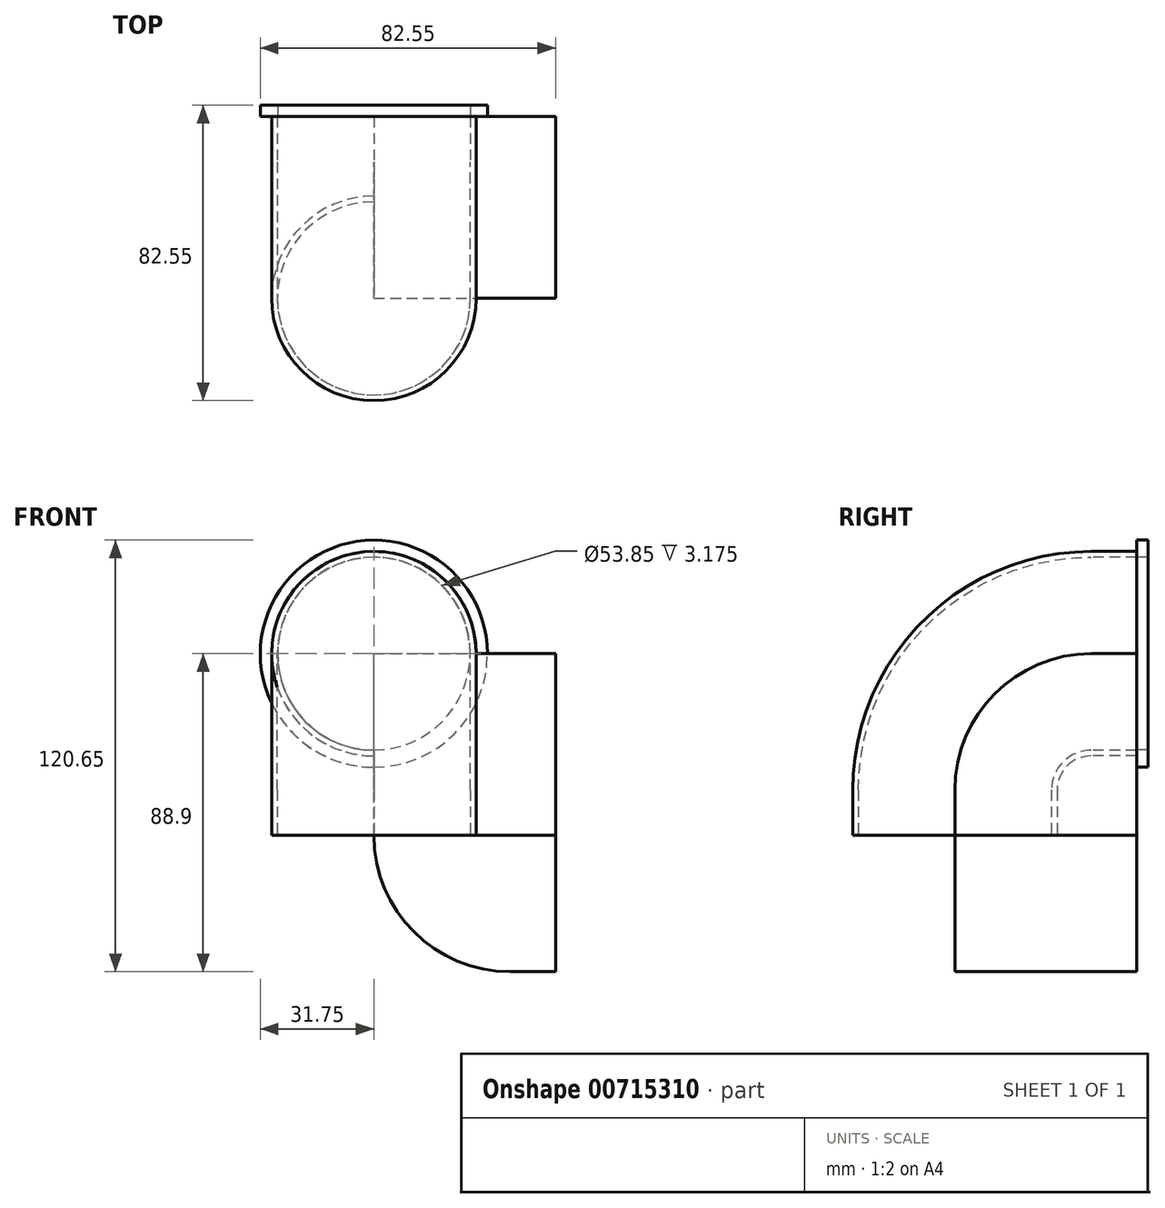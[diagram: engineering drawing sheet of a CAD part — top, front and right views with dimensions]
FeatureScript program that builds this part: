
annotation { "Feature Type Name" : "Feature", "Feature Type Description" : "" }
export const myFeature = defineFeature(function(context is Context, id is Id, definition is map)
    precondition{}
    {
        {
            var Q0;
            Q0=qCreatedBy(makeId("Top.planeOp"),FACE);
            var sketch = newSketch(context, id + "F0", { "sketchPlane" : qUnion([Q0])});
            skLineSegment(sketch, "E0.bottom", {"start": v(-25.4, 25.4) * mm, "end": v(25.4, 25.4) * mm});
            skLineSegment(sketch, "E0.top", {"start": v(-25.4, -25.4) * mm, "end": v(25.4, -25.4) * mm});
            skLineSegment(sketch, "E0.left", {"start": v(-25.4, 25.4) * mm, "end": v(-25.4, -25.4) * mm});
            skLineSegment(sketch, "E0.right", {"start": v(25.4, 25.4) * mm, "end": v(25.4, -25.4) * mm});
            skPoint(sketch, "E0.middle", {"position": v(0, 0) * mm});
            skSolve(sketch);
        }
        {
            var Q0;
            Q0=qSketchRegion(id+"F0",true);
            extrude(context, id + "F1", {"entities" : qUnion([Q0]), "oppositeDirection" : true, "depth" : 50.8 * mm, "offsetDistance" : 25.4 * mm});
        }
        {
            var Q0;
            Q0=makeQuery(id+"F1.opExtrude","CAP_EDGE",EDGE,{"disambiguationData":[OSD([sQuery(id+"F0.wireOp",EDGE,"E0.top")])],"isStart":true});
            fillet(context, id + "F2", {"entities" : qUnion([Q0]), "radius" : 38.1 * mm, "tangentPropagation" : true, "allowEdgeOverflow" : false});
        }
        {
            var Q0;
            Q0=makeQuery(id+"F1.opExtrude","SWEPT_FACE",FACE,{"disambiguationData":[OSD([sQuery(id+"F0.wireOp",EDGE,"E0.bottom")])]});
            var sketch = newSketch(context, id + "F3", { "sketchPlane" : qUnion([Q0])});
            skCircle(sketch, "E1", {"center": v(25.4, 0) * mm, "radius": 28.58 * mm});
            skSolve(sketch);
        }
        {
            var Q0;
            {var subQ0=sQuery(id+"F3.wireOp",EDGE,"E1");var subQ1=sQuery(id+"F0.wireOp",EDGE,"E0.bottom");var subQ4=makeQuery(id+"F1.opExtrude","CAP_EDGE",EDGE,{"disambiguationData":[OSD([subQ1])],"isStart":true});var subQ5=makeQuery(id+"F3.imprint","INTERSECT",VERTEX,{"derivedFrom":[subQ4,subQ0]});Q0=makeQuery(id+"F3.imprint","IMPRINT",FACE,{"disambiguationData":[TD([[makeQuery(id+"F3.imprint","IMPRINT",EDGE,{"disambiguationData":[TD([[subQ5,1.0]])],"derivedFrom":subQ0}),1.0]])]});}
            var Q1;
            {var subQ0=sQuery(id+"F3.wireOp",EDGE,"E1");var subQ1=sQuery(id+"F0.wireOp",EDGE,"E0.bottom");var subQ4=makeQuery(id+"F1.opExtrude","CAP_EDGE",EDGE,{"disambiguationData":[OSD([subQ1])],"isStart":true});var subQ5=makeQuery(id+"F3.imprint","INTERSECT",VERTEX,{"derivedFrom":[subQ4,subQ0]});Q1=makeQuery(id+"F3.imprint","IMPRINT",FACE,{"disambiguationData":[TD([[makeQuery(id+"F3.imprint","IMPRINT",EDGE,{"disambiguationData":[TD([[subQ5,-1.0]])],"derivedFrom":subQ0}),1.0]])]});}
            var Q2;
            Q2=makeQuery(id+"F1.opExtrude","CAP_EDGE",EDGE,{"disambiguationData":[OSD([sQuery(id+"F0.wireOp",EDGE,"E0.left")])],"isStart":true});
            var Q3;
            Q3=makeQuery(id+"F2.opFillet","BLEND_EDGE",EDGE,{"blendedFrom":[makeQuery(id+"F1.opExtrude","CAP_EDGE",EDGE,{"disambiguationData":[OSD([sQuery(id+"F0.wireOp",EDGE,"E0.top")])],"isStart":true}),makeQuery(id+"F1.opExtrude","SWEPT_FACE",FACE,{"disambiguationData":[OSD([sQuery(id+"F0.wireOp",EDGE,"E0.left")])]})],"blendedInto":[makeQuery(id+"F1.opExtrude","SWEPT_FACE",FACE,{"disambiguationData":[OSD([sQuery(id+"F0.wireOp",EDGE,"E0.left")])]})]});
            var Q4;
            Q4=makeQuery(id+"F1.opExtrude","SWEPT_EDGE",EDGE,{"disambiguationData":[OSD([sQuery(id+"F0.wireOp",EDGE,"E0.top"),sQuery(id+"F0.wireOp",EDGE,"E0.left")])]});
            sweep(context, id + "F4", {"profiles" : qUnion([Q0, Q1]), "path" : qUnion([Q2, Q3, Q4])});
        }
        {
            var Q0;
            Q0=makeQuery(id+"F1.opExtrude","CAP_FACE",FACE,{"disambiguationData":[OSD([sQuery(id+"F0.wireOp",EDGE,"E0.bottom"),sQuery(id+"F0.wireOp",EDGE,"E0.top"),sQuery(id+"F0.wireOp",EDGE,"E0.left"),sQuery(id+"F0.wireOp",EDGE,"E0.right")])],"isStart":false});
            var sketch = newSketch(context, id + "F5", { "sketchPlane" : qUnion([Q0])});
            skLineSegment(sketch, "E2.bottom", {"start": v(-25.4, 25.4) * mm, "end": v(25.4, 25.4) * mm});
            skLineSegment(sketch, "E2.top", {"start": v(-25.4, -25.4) * mm, "end": v(25.4, -25.4) * mm});
            skLineSegment(sketch, "E2.left", {"start": v(-25.4, 25.4) * mm, "end": v(-25.4, -25.4) * mm});
            skLineSegment(sketch, "E2.right", {"start": v(25.4, 25.4) * mm, "end": v(25.4, -25.4) * mm});
            skPoint(sketch, "E2.middle", {"position": v(0, 0) * mm});
            skSolve(sketch);
        }
        {
            var Q0;
            Q0=qSketchRegion(id+"F5",true);
            extrude(context, id + "F6", {"entities" : qUnion([Q0]), "depth" : 38.1 * mm, "offsetDistance" : 25.4 * mm});
        }
        {
            var Q0;
            Q0=makeQuery(id+"F6.opExtrude","CAP_EDGE",EDGE,{"disambiguationData":[OSD([sQuery(id+"F5.wireOp",EDGE,"E2.left")])],"isStart":false});
            fillet(context, id + "F7", {"entities" : qUnion([Q0]), "radius" : 38.1 * mm, "tangentPropagation" : true, "allowEdgeOverflow" : false});
        }
        {
            var Q0;
            Q0=makeQuery(id+"F4.opSweep","CAP_FACE",FACE,{"disambiguationData":[OSD([sQuery(id+"F0.wireOp",EDGE,"E0.bottom"),sQuery(id+"F0.wireOp",EDGE,"E0.top"),sQuery(id+"F0.wireOp",EDGE,"E0.left"),sQuery(id+"F0.wireOp",EDGE,"E0.right"),sQuery(id+"F3.wireOp",EDGE,"E1")])],"isStart":false});
            var Q1;
            Q1=makeQuery(id+"F4.opSweep","CAP_FACE",FACE,{"disambiguationData":[OSD([sQuery(id+"F0.wireOp",EDGE,"E0.bottom"),sQuery(id+"F0.wireOp",EDGE,"E0.left"),sQuery(id+"F3.wireOp",EDGE,"E1")])],"isStart":true});
            shell(context, id + "F8", {"entities" : qUnion([Q0, Q1]), "thickness" : 1.59 * mm});
        }
        {
            var Q0;
            Q0=makeQuery(id+"F4.opSweep","CAP_FACE",FACE,{"disambiguationData":[OSD([sQuery(id+"F0.wireOp",EDGE,"E0.bottom"),sQuery(id+"F0.wireOp",EDGE,"E0.left"),sQuery(id+"F3.wireOp",EDGE,"E1")])],"isStart":true});
            var sketch = newSketch(context, id + "F9", { "sketchPlane" : qUnion([Q0])});
            skCircle(sketch, "E3", {"center": v(25.4, 0) * mm, "radius": 31.75 * mm});
            skCircle(sketch, "E4", {"center": v(25.4, 0) * mm, "radius": 26.92 * mm});
            skSolve(sketch);
        }
        {
            var Q0;
            Q0=qSketchRegion(id+"F9",true);
            extrude(context, id + "F10", {"entities" : qUnion([Q0]), "operationType" : NewBodyOperationType.ADD, "depth" : 3.17 * mm, "offsetDistance" : 25.4 * mm});
        }
    });
